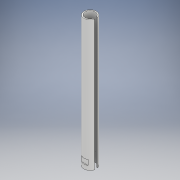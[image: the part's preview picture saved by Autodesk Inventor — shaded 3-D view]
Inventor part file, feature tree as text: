
AUTODESK INVENTOR PART (.ipt)
format: ipt  version: 2017 (Build 210142000, 142)  size: 136,704 bytes
history: native  units: mm
features: extrude x3, sketch x3, plane x1
ambient origin geometry x8: Origin, YZ Plane, XZ Plane, XY Plane, X Axis, Y Axis, Z Axis, Center Point
bodies: Solid1 (feature_tree)
feature tree (7):
  extrude  "Extrusion1"  Depth=3.73mm
  plane  "Work Plane1"
  extrude  "Extrusion4"  [1 undecoded]
  extrude  "Extrusion5"  Depth=17.5mm TaperAngle=0.0deg
  sketch  "Sketch1"  dims[d0=42.16mm d1=3.73mm]
  sketch  "Sketch6"  dims[d2=445.0mm d3=0.0mm d9=-413.0mm]
  sketch  "Sketch7"  dims[d10=18.0mm d11=17.5mm d12=0.0mm d13=30.0mm d14=11.5mm d15=0.0mm d16=0.0mm]
note: 1 required parameter value undecoded (feature->parameter linkage not recoverable at this tier; creation-order binding heuristic only, values carry confidence <= 0.55)
